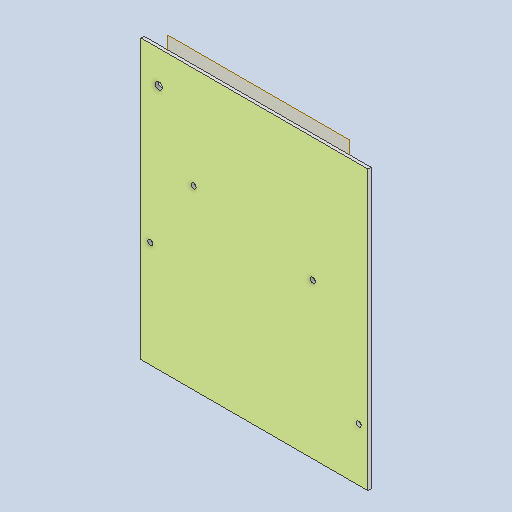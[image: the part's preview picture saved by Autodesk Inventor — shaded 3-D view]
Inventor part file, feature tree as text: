
AUTODESK INVENTOR PART (.ipt)
format: ipt  version: 2023.2 (Build 272271000, 271)  size: 181,760 bytes
history: native  units: mm
features: other x6, reference x6, hole x3, sketch x2, plane x1, extrude x1
ambient origin geometry x8: Origin, YZ Plane, XZ Plane, XY Plane, X Axis, Y Axis, Z Axis, Center Point
bodies: Body1 (feature_tree)
feature tree (19):
  other  "Z axis front plate"
  plane  "Work Plane1"
  extrude  "Extrusion1"  Depth=3.0mm
  hole  "Hole1"  [1 undecoded]
  hole  "Hole3"  [1 undecoded]
  hole  "Hole4"  [1 undecoded]
  reference  "Reference1"
  reference  "Reference2"
  sketch  "Sketch3"  dims[d1=3.0mm d2=0.0mm d4=33.0mm]
  reference  "Reference3"
  reference  "Reference4"
  reference  "Reference5"
  reference  "Reference6"
  sketch  "Sketch4"  dims[d5=5.1mm d6=6.0mm d7=4.0mm d8=2.0mm d9=90.0deg d10=8.0mm d11=20.594885mm d12=150.0mm d14=11.0mm d15=11.0mm d16=13.7mm d24=5.1mm d25=6.0mm d26=4.0mm d27=2.0mm d28=90.0deg d29=8.0mm d30=20.594885mm d31=7.1mm d32=6.0mm d33=4.0mm d34=2.0mm d35=90.0deg d36=8.0mm d37=20.594885mm d39=11.0mm d40=20.0mm d41=90.0deg d13=0.0625mm]
  parser-record x1  (decoder bookkeeping rows leaked as tree rows — omitted from the tree; the rows remain in map.json)
  other  "Main Assembly.iam"
  other  "Z axis Back Plate:1"
  other  "20x20-V-Slot-Extrusion:1"
  other  "20x20-V-Slot-Extrusion:2"
note: 3 required parameter values undecoded (feature->parameter linkage not recoverable at this tier; creation-order binding heuristic only, values carry confidence <= 0.55)
note: 1 file-system path scrubbed to <path> (originals preserved in map.json)
